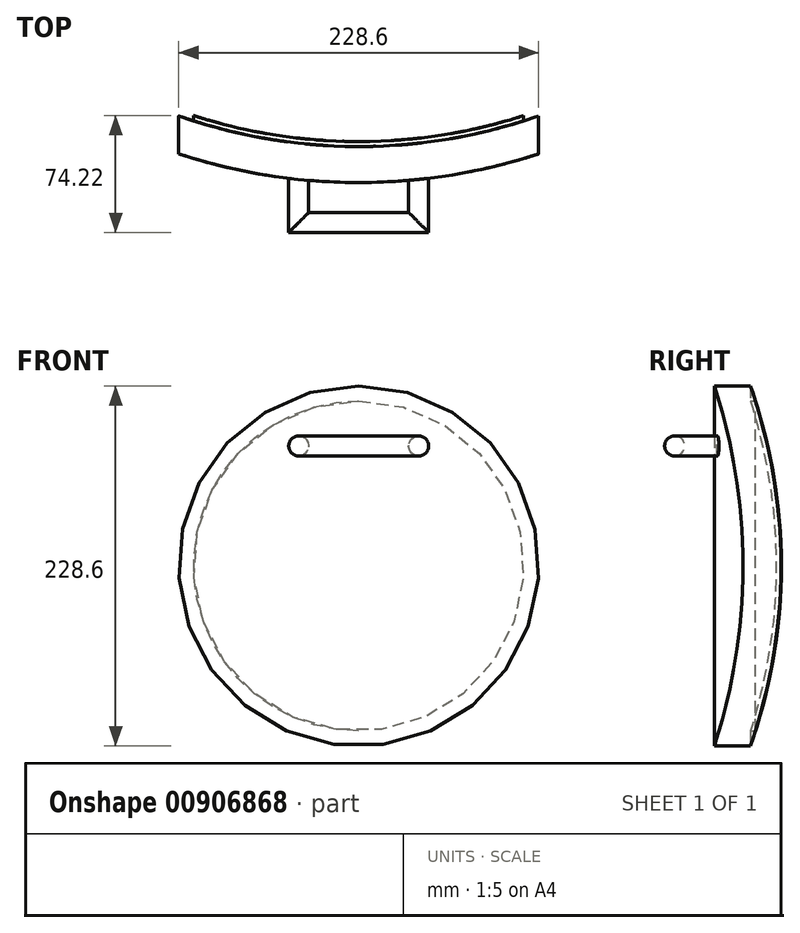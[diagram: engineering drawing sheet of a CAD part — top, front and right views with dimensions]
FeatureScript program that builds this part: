
annotation { "Feature Type Name" : "Feature", "Feature Type Description" : "" }
export const myFeature = defineFeature(function(context is Context, id is Id, definition is map)
    precondition{}
    {
        {
            var Q0;
            Q0=qCreatedBy(makeId("Top.planeOp"),FACE);
            var sketch = newSketch(context, id + "F0", { "sketchPlane" : qUnion([Q0])});
            skArc(sketch, "E0", {"start": v(-104.77, -325.83) * mm, "mid": v(0, -342.27) * mm, "end": v(104.77, -325.83) * mm});
            skArc(sketch, "E1", {"start": v(-104.77, -329.17) * mm, "mid": v(0, -345.44) * mm, "end": v(104.78, -329.17) * mm});
            skLineSegment(sketch, "E2", {"start": v(0, 0) * mm, "end": v(0, -383.86) * mm, "construction": true});
            skLineSegment(sketch, "E3", {"start": v(-104.78, -329.17) * mm, "end": v(-104.78, -325.83) * mm});
            skLineSegment(sketch, "E4", {"start": v(104.78, -329.17) * mm, "end": v(104.78, -325.83) * mm});
            skPoint(sketch, "E5.MirrorCS.start.orphan", {"position": v(0, -383.86) * mm});
            skSolve(sketch);
        }
        {
            var Q0;
            Q0 = qSketchRegion(id + "F0", true);
            extrude(context, id + "F1", {"entities" : qUnion([Q0]), "endBound" : BoundingType.SYMMETRIC, "oppositeDirection" : true, "depth" : 209.55 * mm, "offsetDistance" : 25.4 * mm});
        }
        {
            var Q0;
            Q0=qCreatedBy(makeId("Front.planeOp"),FACE);
            var sketch = newSketch(context, id + "F2", { "sketchPlane" : qUnion([Q0])});
            skCircle(sketch, "E6", {"center": v(0, 0) * mm, "radius": 104.78 * mm});
            skCircle(sketch, "E7", {"center": v(0, 0) * mm, "radius": 159.23 * mm});
            skSolve(sketch);
        }
        {
            var Q0;
            Q0 = qSketchRegion(id + "F2", true);
            extrude(context, id + "F3", {"entities" : qUnion([Q0]), "operationType" : NewBodyOperationType.REMOVE, "depth" : 414.02 * mm, "offsetDistance" : 25.4 * mm});
        }
        {
            var Q0;
            Q0=qCreatedBy(makeId("Top.planeOp"),FACE);
            var sketch = newSketch(context, id + "F4", { "sketchPlane" : qUnion([Q0])});
            skArc(sketch, "E8", {"start": v(-114.3, -350.11) * mm, "mid": v(0, -368.3) * mm, "end": v(114.3, -350.11) * mm});
            skArc(sketch, "E9", {"start": v(-114.3, -325.98) * mm, "mid": v(0, -345.44) * mm, "end": v(114.3, -325.98) * mm});
            skLineSegment(sketch, "E10", {"start": v(0, 0) * mm, "end": v(0, -462.28) * mm, "construction": true});
            skLineSegment(sketch, "E11", {"start": v(-114.3, -350.11) * mm, "end": v(-114.3, -325.98) * mm});
            skLineSegment(sketch, "E12", {"start": v(114.3, -350.11) * mm, "end": v(114.3, -325.98) * mm});
            skSolve(sketch);
        }
        {
            var Q0;
            Q0 = qSketchRegion(id + "F4", true);
            extrude(context, id + "F5", {"entities" : qUnion([Q0]), "operationType" : NewBodyOperationType.ADD, "endBound" : BoundingType.SYMMETRIC, "depth" : 228.6 * mm, "offsetDistance" : 25.4 * mm});
        }
        {
            var Q0;
            Q0=qCreatedBy(makeId("Front.planeOp"),FACE);
            var sketch = newSketch(context, id + "F6", { "sketchPlane" : qUnion([Q0])});
            skCircle(sketch, "E13", {"center": v(0, 0) * mm, "radius": 114.3 * mm});
            skCircle(sketch, "E14", {"center": v(0, 0) * mm, "radius": 184.3 * mm});
            skSolve(sketch);
        }
        {
            var Q0;
            Q0 = qSketchRegion(id + "F6", true);
            extrude(context, id + "F7", {"entities" : qUnion([Q0]), "operationType" : NewBodyOperationType.REMOVE, "depth" : 563.88 * mm, "offsetDistance" : 25.4 * mm});
        }
        {
            var Q0;
            Q0=qCreatedBy(makeId("Front.planeOp"),FACE);
            cPlane(context, id + "F8", {"entities" : qUnion([Q0]), "cplaneType" : CPlaneType.OFFSET, "offset" : 355.6 * mm, "width" : 152.4 * mm, "height" : 152.4 * mm});
        }
        {
            var Q0;
            Q0=qCreatedBy(id+"F8.planeOp",FACE);
            var sketch = newSketch(context, id + "F9", { "sketchPlane" : qUnion([Q0])});
            skLineSegment(sketch, "E15", {"start": v(0, 0) * mm, "end": v(0, 122.67) * mm, "construction": true});
            skLineSegment(sketch, "E16", {"start": v(0, 76.2) * mm, "end": v(-38.1, 76.2) * mm, "construction": true});
            skCircle(sketch, "E17", {"center": v(-38.1, 76.2) * mm, "radius": 6.35 * mm});
            skSolve(sketch);
        }
        {
            var Q0;
            Q0=qCreatedBy(makeId("Top.planeOp"),FACE);
            cPlane(context, id + "F10", {"entities" : qUnion([Q0]), "cplaneType" : CPlaneType.OFFSET, "offset" : 76.2 * mm, "width" : 152.4 * mm, "height" : 152.4 * mm});
        }
        {
            var Q0;
            Q0=qCreatedBy(id+"F10.planeOp",FACE);
            var sketch = newSketch(context, id + "F11", { "sketchPlane" : qUnion([Q0])});
            skLineSegment(sketch, "E18", {"start": v(0, 0) * mm, "end": v(0, -415.79) * mm, "construction": true});
            skLineSegment(sketch, "E19", {"start": v(0, -393.7) * mm, "end": v(-38.1, -393.7) * mm});
            skLineSegment(sketch, "E20", {"start": v(-38.1, -393.7) * mm, "end": v(-38.1, -353.23) * mm});
            skLineSegment(sketch, "E21.MirrorCS", {"start": v(38.1, -393.7) * mm, "end": v(38.1, -353.23) * mm});
            skLineSegment(sketch, "E22.MirrorCS", {"start": v(0, -393.7) * mm, "end": v(38.1, -393.7) * mm});
            skSolve(sketch);
        }
        {
            var Q0;
            Q0 = qSketchRegion(id + "F9", true);
            var Q1;
            Q1=sQuery(id+"F11.wireOp",EDGE,"E20");
            var Q2;
            Q2=sQuery(id+"F11.wireOp",EDGE,"E19");
            var Q3;
            Q3=sQuery(id+"F11.wireOp",EDGE,"E22.MirrorCS");
            var Q4;
            Q4=sQuery(id+"F11.wireOp",EDGE,"E21.MirrorCS");
            sweep(context, id + "F12", {"operationType" : NewBodyOperationType.ADD, "profiles" : qUnion([Q0]), "path" : qUnion([Q1, Q2, Q3, Q4])});
        }
    });
